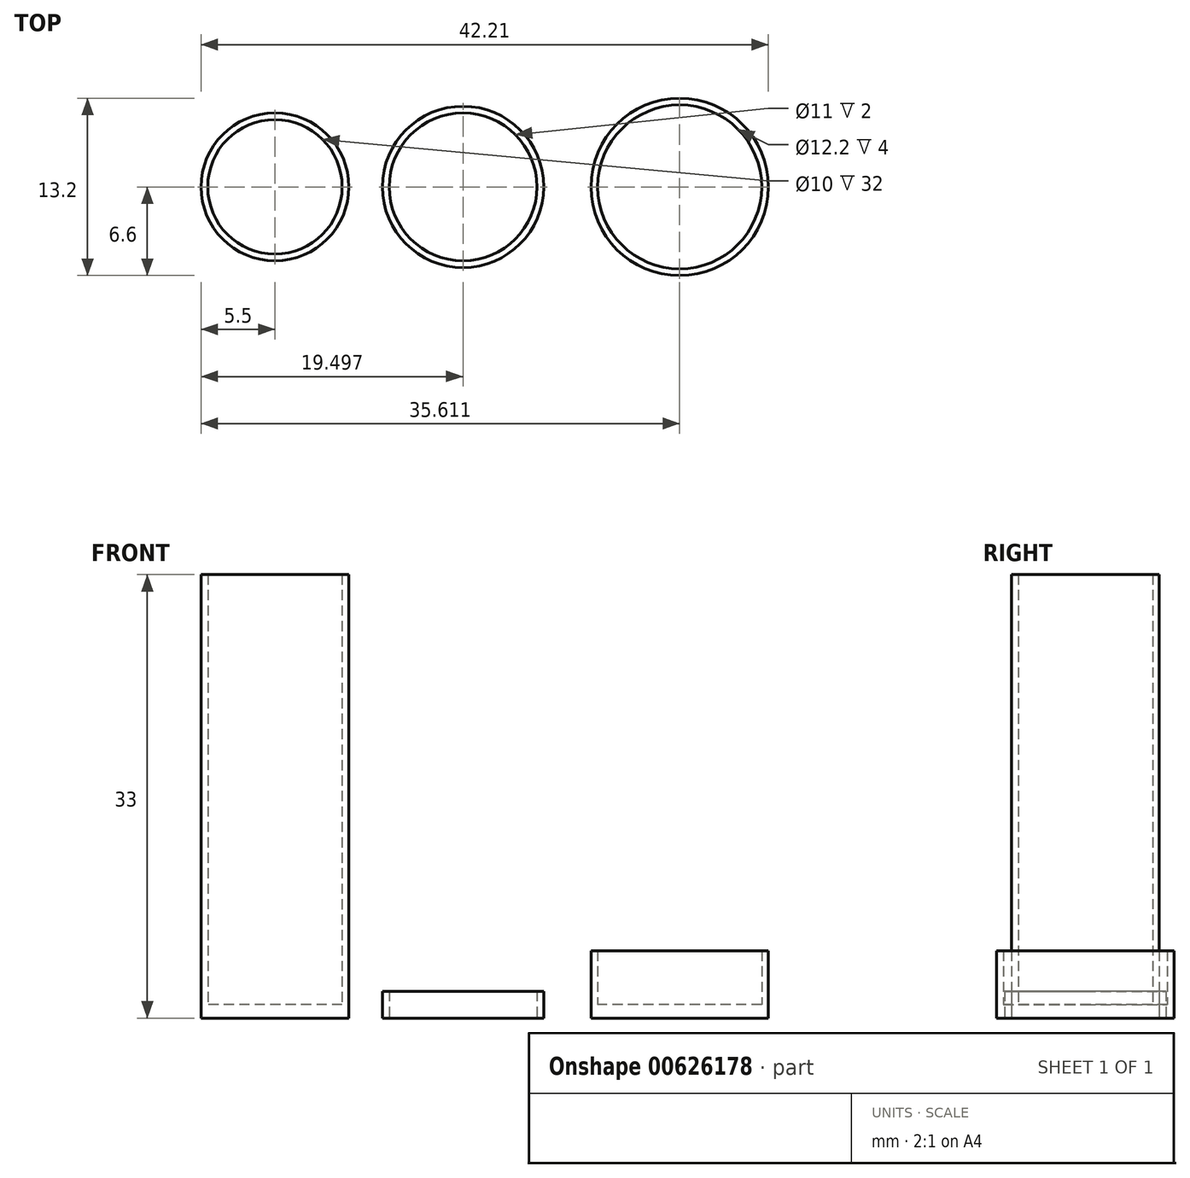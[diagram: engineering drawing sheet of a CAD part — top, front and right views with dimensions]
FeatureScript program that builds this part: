
annotation { "Feature Type Name" : "Feature", "Feature Type Description" : "" }
export const myFeature = defineFeature(function(context is Context, id is Id, definition is map)
    precondition{}
    {
        {
            var Q0;
            Q0=qCreatedBy(makeId("Top.planeOp"),FACE);
            var sketch = newSketch(context, id + "F0", { "sketchPlane" : qUnion([Q0])});
            skCircle(sketch, "E0", {"center": v(0, 0) * mm, "radius": 5 * mm});
            skCircle(sketch, "E1", {"center": v(0, 0) * mm, "radius": 5.5 * mm});
            skCircle(sketch, "E2", {"center": v(14, 0) * mm, "radius": 6 * mm});
            skCircle(sketch, "E3", {"center": v(14, 0) * mm, "radius": 5.5 * mm});
            skCircle(sketch, "E4", {"center": v(30.11, 0) * mm, "radius": 6.1 * mm});
            skCircle(sketch, "E5", {"center": v(30.11, 0) * mm, "radius": 6.6 * mm});
            skSolve(sketch);
        }
        {
            var Q0;
            Q0=makeQuery(id+"F0.imprint","IMPRINT",FACE,{"disambiguationData":[TD([[makeQuery(id+"F0.imprint","IMPRINT",EDGE,{"derivedFrom":sQuery(id+"F0.wireOp",EDGE,"E0")}),-1.0]])]});
            extrude(context, id + "F1", {"entities" : qUnion([Q0]), "depth" : 33 * mm, "offsetDistance" : 25 * mm});
        }
        {
            var Q0;
            Q0=makeQuery(id+"F0.imprint","IMPRINT",FACE,{"disambiguationData":[TD([[makeQuery(id+"F0.imprint","IMPRINT",EDGE,{"derivedFrom":sQuery(id+"F0.wireOp",EDGE,"E0")}),1.0]])]});
            extrude(context, id + "F2", {"entities" : qUnion([Q0]), "operationType" : NewBodyOperationType.ADD, "depth" : 1 * mm, "offsetDistance" : 25 * mm});
        }
        {
            var Q0;
            Q0=makeQuery(id+"F0.imprint","IMPRINT",FACE,{"disambiguationData":[TD([[makeQuery(id+"F0.imprint","IMPRINT",EDGE,{"derivedFrom":sQuery(id+"F0.wireOp",EDGE,"E2")}),1.0]])]});
            extrude(context, id + "F3", {"entities" : qUnion([Q0]), "depth" : 2 * mm, "offsetDistance" : 25 * mm});
        }
        {
            var Q0;
            Q0=makeQuery(id+"F0.imprint","IMPRINT",FACE,{"disambiguationData":[TD([[makeQuery(id+"F0.imprint","IMPRINT",EDGE,{"derivedFrom":sQuery(id+"F0.wireOp",EDGE,"E4")}),-1.0]])]});
            extrude(context, id + "F4", {"entities" : qUnion([Q0]), "depth" : 5 * mm, "offsetDistance" : 25 * mm});
        }
        {
            var Q0;
            Q0=makeQuery(id+"F0.imprint","IMPRINT",FACE,{"disambiguationData":[TD([[makeQuery(id+"F0.imprint","IMPRINT",EDGE,{"derivedFrom":sQuery(id+"F0.wireOp",EDGE,"E4")}),1.0]])]});
            extrude(context, id + "F5", {"entities" : qUnion([Q0]), "operationType" : NewBodyOperationType.ADD, "depth" : 1 * mm, "offsetDistance" : 25 * mm});
        }
    });
